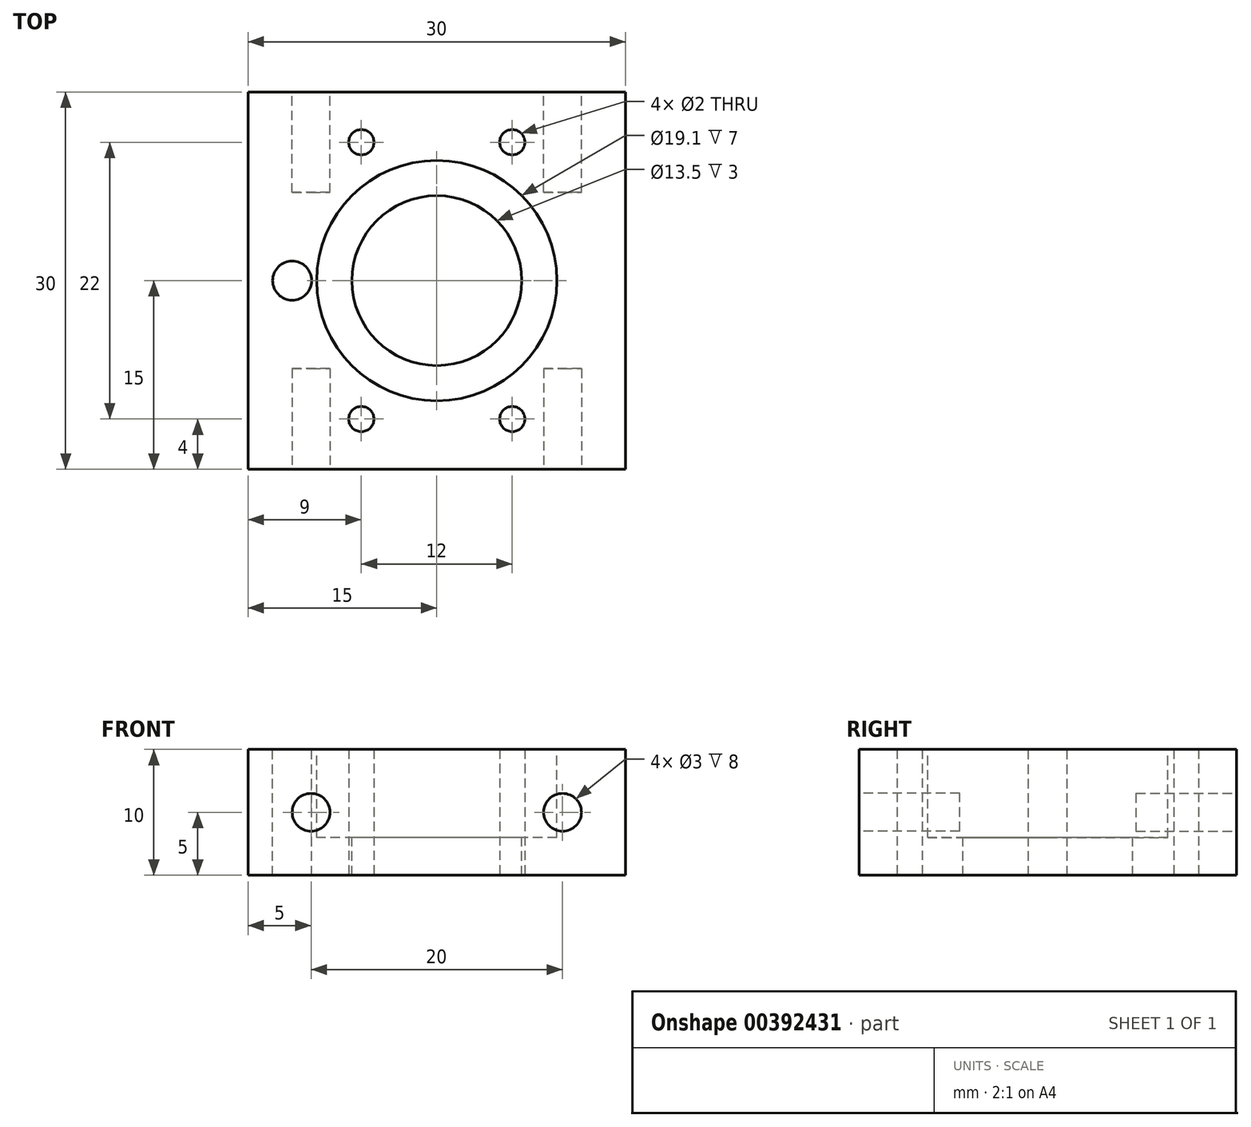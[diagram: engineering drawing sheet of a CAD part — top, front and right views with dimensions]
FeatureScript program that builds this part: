
annotation { "Feature Type Name" : "Feature", "Feature Type Description" : "" }
export const myFeature = defineFeature(function(context is Context, id is Id, definition is map)
    precondition{}
    {
        {
            var Q0;
            Q0=qCreatedBy(makeId("Top.planeOp"),FACE);
            var sketch = newSketch(context, id + "F0", { "sketchPlane" : qUnion([Q0])});
            skLineSegment(sketch, "E0.bottom", {"start": v(0, 0) * mm, "end": v(30, 0) * mm});
            skLineSegment(sketch, "E0.top", {"start": v(0, -30) * mm, "end": v(30, -30) * mm});
            skLineSegment(sketch, "E0.left", {"start": v(0, 0) * mm, "end": v(0, -30) * mm});
            skLineSegment(sketch, "E0.right", {"start": v(30, 0) * mm, "end": v(30, -30) * mm});
            skSolve(sketch);
        }
        {
            var Q0;
            Q0=makeQuery(id+"F0.imprint","IMPRINT",FACE,{"disambiguationData":[TD([[makeQuery(id+"F0.imprint","IMPRINT",EDGE,{"derivedFrom":sQuery(id+"F0.wireOp",EDGE,"E0.bottom")}),-1.0]])]});
            extrude(context, id + "F1", {"entities" : qUnion([Q0]), "oppositeDirection" : true, "depth" : 10 * mm});
        }
        {
            var Q0;
            Q0=makeQuery(id+"F1.opExtrude","CAP_FACE",FACE,{"disambiguationData":[OSD([sQuery(id+"F0.wireOp",EDGE,"E0.bottom"),sQuery(id+"F0.wireOp",EDGE,"E0.top"),sQuery(id+"F0.wireOp",EDGE,"E0.left"),sQuery(id+"F0.wireOp",EDGE,"E0.right")])],"isStart":true});
            var sketch = newSketch(context, id + "F2", { "sketchPlane" : qUnion([Q0])});
            skCircle(sketch, "E1", {"center": v(15, -15) * mm, "radius": 9.55 * mm});
            skSolve(sketch);
        }
        {
            var Q0;
            Q0=makeQuery(id+"F2.imprint","IMPRINT",FACE,{"disambiguationData":[TD([[makeQuery(id+"F2.imprint","IMPRINT",EDGE,{"derivedFrom":sQuery(id+"F2.wireOp",EDGE,"E1")}),1.0]])]});
            extrude(context, id + "F3", {"entities" : qUnion([Q0]), "operationType" : NewBodyOperationType.REMOVE, "oppositeDirection" : true, "depth" : 7 * mm});
        }
        {
            var Q0;
            Q0=makeQuery(id+"F3.boolean.opBoolean","COPY",FACE,{"derivedFrom":makeQuery(id+"F3.opExtrude","CAP_FACE",FACE,{"disambiguationData":[OSD([sQuery(id+"F2.wireOp",EDGE,"E1")])],"isStart":false})});
            var sketch = newSketch(context, id + "F4", { "sketchPlane" : qUnion([Q0])});
            skCircle(sketch, "E2", {"center": v(15, -15) * mm, "radius": 6.75 * mm});
            skSolve(sketch);
        }
        {
            var Q0;
            Q0=makeQuery(id+"F4.imprint","IMPRINT",FACE,{"disambiguationData":[TD([[makeQuery(id+"F4.imprint","IMPRINT",EDGE,{"derivedFrom":sQuery(id+"F4.wireOp",EDGE,"E2")}),1.0]])]});
            extrude(context, id + "F5", {"entities" : qUnion([Q0]), "operationType" : NewBodyOperationType.REMOVE, "endBound" : BoundingType.UP_TO_NEXT, "oppositeDirection" : true, "depth" : 25 * mm});
        }
        {
            var Q0;
            Q0=makeQuery(id+"F1.opExtrude","CAP_FACE",FACE,{"disambiguationData":[OSD([sQuery(id+"F0.wireOp",EDGE,"E0.bottom"),sQuery(id+"F0.wireOp",EDGE,"E0.top"),sQuery(id+"F0.wireOp",EDGE,"E0.left"),sQuery(id+"F0.wireOp",EDGE,"E0.right")])],"isStart":true});
            var sketch = newSketch(context, id + "F6", { "sketchPlane" : qUnion([Q0])});
            skCircle(sketch, "E3", {"center": v(3.5, -15) * mm, "radius": 1.55 * mm});
            skLineSegment(sketch, "E4", {"start": v(3.5, -15) * mm, "end": v(0, -15) * mm});
            skSolve(sketch);
        }
        {
            var Q0;
            {var subQ0=sQuery(id+"F6.wireOp",EDGE,"E3");var subQ1=makeQuery(id+"F6.imprint","IMPRINT",VERTEX,{"derivedFrom":subQ0});Q0=makeQuery(id+"F6.imprint","IMPRINT",FACE,{"disambiguationData":[TD([[makeQuery(id+"F6.imprint","IMPRINT",EDGE,{"disambiguationData":[TD([[subQ1,1.0]])],"derivedFrom":subQ0}),1.0]])]});}
            var Q1;
            {var subQ0=sQuery(id+"F6.wireOp",EDGE,"E3");var subQ1=makeQuery(id+"F3.boolean.opBoolean","COPY",EDGE,{"derivedFrom":makeQuery(id+"F3.opExtrude","CAP_EDGE",EDGE,{"disambiguationData":[OSD([sQuery(id+"F2.wireOp",EDGE,"E1")])],"isStart":true})});var subQ2=makeQuery(id+"F6.imprint","INTERSECT",VERTEX,{"disambiguationData":[OD(0.0)],"derivedFrom":[subQ1,subQ0]});Q1=makeQuery(id+"F6.imprint","IMPRINT",FACE,{"disambiguationData":[TD([[makeQuery(id+"F6.imprint","IMPRINT",EDGE,{"disambiguationData":[TD([[subQ2,1.0]])],"derivedFrom":subQ0}),1.0]])]});}
            extrude(context, id + "F7", {"entities" : qUnion([Q0, Q1]), "operationType" : NewBodyOperationType.REMOVE, "endBound" : BoundingType.UP_TO_NEXT, "oppositeDirection" : true, "depth" : 25 * mm});
        }
        {
            var Q0;
            Q0=makeQuery(id+"F1.opExtrude","SWEPT_FACE",FACE,{"disambiguationData":[OSD([sQuery(id+"F0.wireOp",EDGE,"E0.top")])]});
            var sketch = newSketch(context, id + "F8", { "sketchPlane" : qUnion([Q0])});
            skCircle(sketch, "E5", {"center": v(5, -5) * mm, "radius": 1.5 * mm});
            skPoint(sketch, "E5.centerSnap0", {"position": v(0, -5) * mm});
            skCircle(sketch, "E6", {"center": v(25, -5) * mm, "radius": 1.5 * mm});
            skPoint(sketch, "E6.centerSnap0", {"position": v(30, -5) * mm});
            skSolve(sketch);
        }
        {
            var Q0;
            Q0=makeQuery(id+"F8.imprint","IMPRINT",FACE,{"disambiguationData":[TD([[makeQuery(id+"F8.imprint","IMPRINT",EDGE,{"derivedFrom":sQuery(id+"F8.wireOp",EDGE,"E5")}),1.0]])]});
            var Q1;
            Q1=makeQuery(id+"F8.imprint","IMPRINT",FACE,{"disambiguationData":[TD([[makeQuery(id+"F8.imprint","IMPRINT",EDGE,{"derivedFrom":sQuery(id+"F8.wireOp",EDGE,"E6")}),1.0]])]});
            extrude(context, id + "F9", {"entities" : qUnion([Q0, Q1]), "operationType" : NewBodyOperationType.REMOVE, "oppositeDirection" : true, "depth" : 8 * mm});
        }
        {
            var Q0;
            Q0=makeQuery(id+"F1.opExtrude","SWEPT_FACE",FACE,{"disambiguationData":[OSD([sQuery(id+"F0.wireOp",EDGE,"E0.bottom")])]});
            var sketch = newSketch(context, id + "F10", { "sketchPlane" : qUnion([Q0])});
            skCircle(sketch, "E7", {"center": v(-25, -5) * mm, "radius": 1.5 * mm});
            skPoint(sketch, "E7.centerSnap0", {"position": v(-30, -5) * mm});
            skCircle(sketch, "E8", {"center": v(-5, -5) * mm, "radius": 1.5 * mm});
            skPoint(sketch, "E8.centerSnap0", {"position": v(0, -5) * mm});
            skSolve(sketch);
        }
        {
            var Q0;
            Q0=makeQuery(id+"F10.imprint","IMPRINT",FACE,{"disambiguationData":[TD([[makeQuery(id+"F10.imprint","IMPRINT",EDGE,{"derivedFrom":sQuery(id+"F10.wireOp",EDGE,"E7")}),1.0]])]});
            var Q1;
            Q1=makeQuery(id+"F10.imprint","IMPRINT",FACE,{"disambiguationData":[TD([[makeQuery(id+"F10.imprint","IMPRINT",EDGE,{"derivedFrom":sQuery(id+"F10.wireOp",EDGE,"E8")}),1.0]])]});
            extrude(context, id + "F11", {"entities" : qUnion([Q0, Q1]), "operationType" : NewBodyOperationType.REMOVE, "oppositeDirection" : true, "depth" : 8 * mm});
        }
        {
            var Q0;
            Q0=makeQuery(id+"F1.opExtrude","CAP_FACE",FACE,{"disambiguationData":[OSD([sQuery(id+"F0.wireOp",EDGE,"E0.bottom"),sQuery(id+"F0.wireOp",EDGE,"E0.top"),sQuery(id+"F0.wireOp",EDGE,"E0.left"),sQuery(id+"F0.wireOp",EDGE,"E0.right")])],"isStart":false});
            var sketch = newSketch(context, id + "F12", { "sketchPlane" : qUnion([Q0])});
            skLineSegment(sketch, "E9", {"start": v(15, 15) * mm, "end": v(21, 15) * mm});
            skCircle(sketch, "E10", {"center": v(21, 26) * mm, "radius": 1 * mm});
            skCircle(sketch, "E11", {"center": v(9, 26) * mm, "radius": 1 * mm});
            skCircle(sketch, "E12", {"center": v(9, 4) * mm, "radius": 1 * mm});
            skCircle(sketch, "E13", {"center": v(21, 4) * mm, "radius": 1 * mm});
            skSolve(sketch);
        }
        {
            var Q0;
            Q0=makeQuery(id+"F12.imprint","IMPRINT",FACE,{"disambiguationData":[TD([[makeQuery(id+"F12.imprint","IMPRINT",EDGE,{"derivedFrom":sQuery(id+"F12.wireOp",EDGE,"E12")}),1.0]])]});
            var Q1;
            Q1=makeQuery(id+"F12.imprint","IMPRINT",FACE,{"disambiguationData":[TD([[makeQuery(id+"F12.imprint","IMPRINT",EDGE,{"derivedFrom":sQuery(id+"F12.wireOp",EDGE,"E13")}),1.0]])]});
            var Q2;
            Q2=makeQuery(id+"F12.imprint","IMPRINT",FACE,{"disambiguationData":[TD([[makeQuery(id+"F12.imprint","IMPRINT",EDGE,{"derivedFrom":sQuery(id+"F12.wireOp",EDGE,"E10")}),1.0]])]});
            var Q3;
            Q3=makeQuery(id+"F12.imprint","IMPRINT",FACE,{"disambiguationData":[TD([[makeQuery(id+"F12.imprint","IMPRINT",EDGE,{"derivedFrom":sQuery(id+"F12.wireOp",EDGE,"E11")}),1.0]])]});
            extrude(context, id + "F13", {"entities" : qUnion([Q0, Q1, Q2, Q3]), "operationType" : NewBodyOperationType.REMOVE, "endBound" : BoundingType.UP_TO_NEXT, "oppositeDirection" : true, "depth" : 25 * mm});
        }
    });
